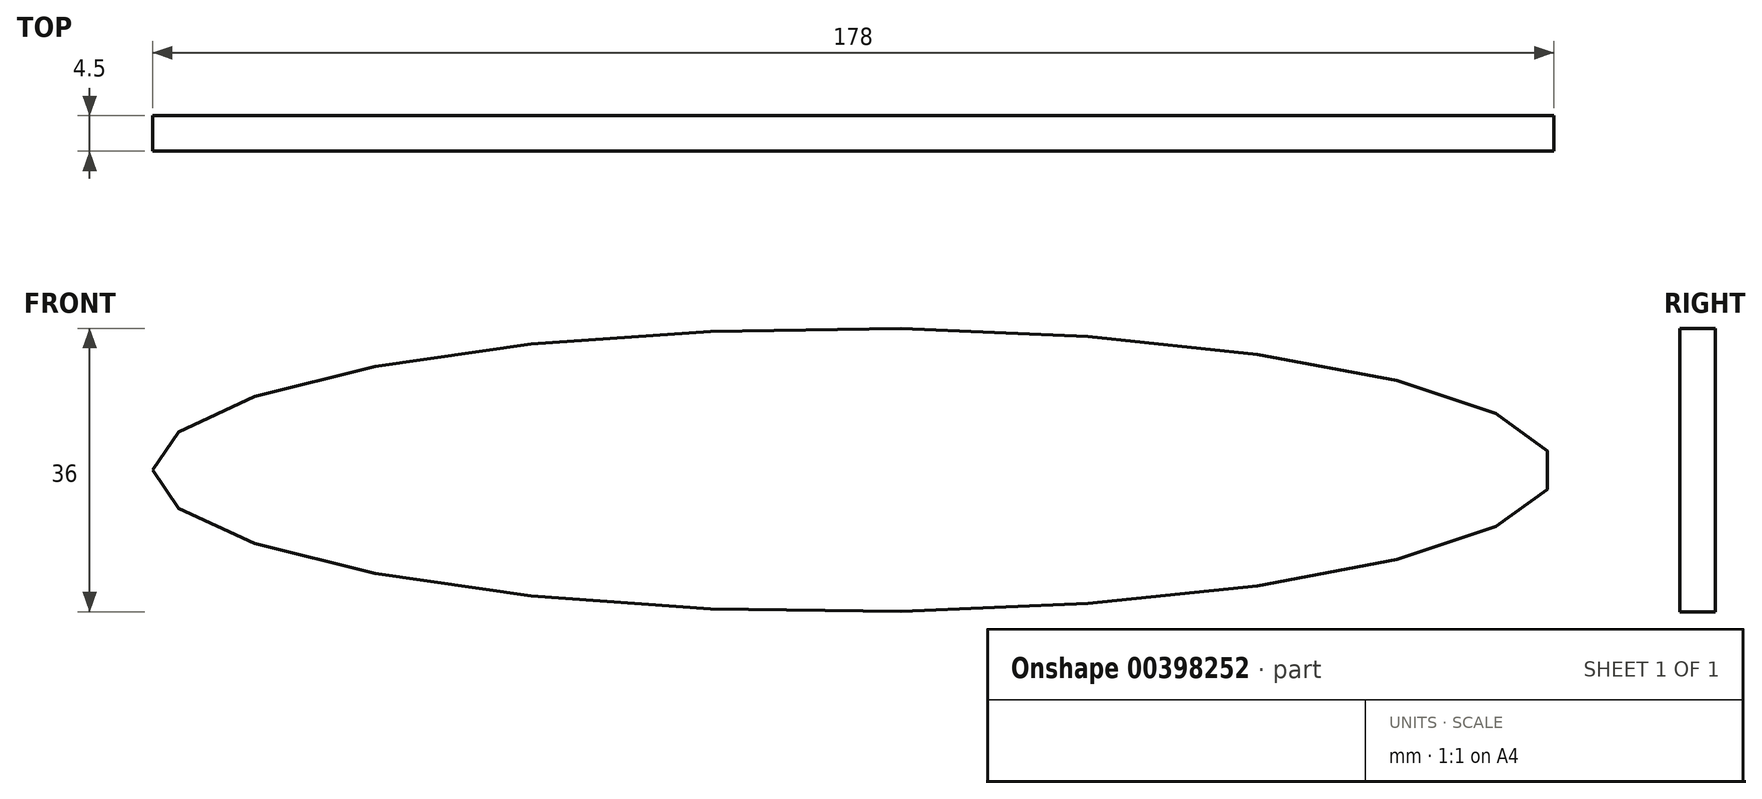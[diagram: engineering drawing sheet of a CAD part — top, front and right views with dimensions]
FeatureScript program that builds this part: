
annotation { "Feature Type Name" : "Feature", "Feature Type Description" : "" }
export const myFeature = defineFeature(function(context is Context, id is Id, definition is map)
    precondition{}
    {
        {
            var Q0;
            Q0=qCreatedBy(makeId("Front.planeOp"),FACE);
            var sketch = newSketch(context, id + "F0", { "sketchPlane" : qUnion([Q0])});
            skEllipse(sketch, "E0", {"center": v(58.81, 0) * mm, "majorRadius": 89 * mm, "minorRadius": 18 * mm, "majorAxis": v(-1, 0)});
            skSolve(sketch);
        }
        {
            var Q0;
            Q0=qSketchRegion(id+"F0",true);
            var Q1;
            Q1=makeQuery(id+"F0.imprint","IMPRINT",FACE,{"disambiguationData":[TD([[makeQuery(id+"F0.imprint","IMPRINT",EDGE,{"derivedFrom":sQuery(id+"F0.wireOp",EDGE,"E0")}),1.0]])]});
            extrude(context, id + "F1", {"entities" : qUnion([Q0, Q1]), "depth" : 1.5 * mm});
        }
        {
            var Q0;
            Q0=qCreatedBy(makeId("Front.planeOp"),FACE);
            var sketch = newSketch(context, id + "F2", { "sketchPlane" : qUnion([Q0])});
            skLineSegment(sketch, "E1", {"start": v(-9.04, 3) * mm, "end": v(11.23, 3) * mm, "construction": true});
            skLineSegment(sketch, "E2", {"start": v(-14.09, 2.99) * mm, "end": v(-14.09, 6.2) * mm});
            skLineSegment(sketch, "E3", {"start": v(-14.09, 6.2) * mm, "end": v(0, 6.2) * mm});
            skLineSegment(sketch, "E4", {"start": v(0, 6.2) * mm, "end": v(0, 10.97) * mm});
            skLineSegment(sketch, "E5", {"start": v(0, 10.97) * mm, "end": v(3.01, 10.97) * mm});
            skLineSegment(sketch, "E6", {"start": v(3.01, 10.97) * mm, "end": v(3.01, 6.2) * mm});
            skLineSegment(sketch, "E7", {"start": v(3.01, 6.2) * mm, "end": v(17.42, 6.2) * mm});
            skLineSegment(sketch, "E8", {"start": v(-14.09, 2.99) * mm, "end": v(17.42, 3) * mm});
            skLineSegment(sketch, "E9", {"start": v(17.42, 3) * mm, "end": v(17.42, 6.2) * mm});
            skLineSegment(sketch, "E10", {"start": v(0, 6.2) * mm, "end": v(0, -11.46) * mm, "construction": true});
            skLineSegment(sketch, "E11", {"start": v(9.3, -3) * mm, "end": v(17.42, -3) * mm});
            skPoint(sketch, "E11.endSnap0", {"position": v(17.42, -3.74) * mm});
            skLineSegment(sketch, "E12", {"start": v(17.42, -3) * mm, "end": v(-14.24, -3) * mm});
            skLineSegment(sketch, "E13", {"start": v(-14.24, -3) * mm, "end": v(-14.09, -6.29) * mm});
            skLineSegment(sketch, "E14", {"start": v(-14.09, -6.29) * mm, "end": v(0, -6.28) * mm});
            skLineSegment(sketch, "E15", {"start": v(0, -6.28) * mm, "end": v(0, -11.46) * mm});
            skLineSegment(sketch, "E16", {"start": v(3.02, -11.46) * mm, "end": v(3.02, -6.28) * mm});
            skLineSegment(sketch, "E17", {"start": v(3.02, -6.28) * mm, "end": v(17.42, -6.27) * mm});
            skLineSegment(sketch, "E18", {"start": v(17.42, -6.27) * mm, "end": v(17.42, -3.74) * mm});
            skLineSegment(sketch, "E19", {"start": v(3.02, -11.46) * mm, "end": v(0, -11.46) * mm});
            skLineSegment(sketch, "E20", {"start": v(17.42, -3.74) * mm, "end": v(17.42, -3) * mm});
            skSolve(sketch);
        }
        {
            var Q0;
            Q0=makeQuery(id+"F1.opExtrude","CAP_FACE",FACE,{"disambiguationData":[OSD([sQuery(id+"F0.wireOp",EDGE,"E0")])],"isStart":false});
            var Q1;
            Q1=makeQuery(id+"FVdWLll0MW8gGsK_1.opExtrude","CAP_FACE",FACE,{"disambiguationData":[OSD([sQuery(id+"F2.wireOp",EDGE,"E2"),sQuery(id+"F2.wireOp",EDGE,"E3"),sQuery(id+"F2.wireOp",EDGE,"E4"),sQuery(id+"F2.wireOp",EDGE,"E5"),sQuery(id+"F2.wireOp",EDGE,"E6"),sQuery(id+"F2.wireOp",EDGE,"E7"),sQuery(id+"F2.wireOp",EDGE,"E8"),sQuery(id+"F2.wireOp",EDGE,"E9")])],"isStart":false});
            extrude(context, id + "F3", {"entities" : qUnion([Q0, Q1]), "operationType" : NewBodyOperationType.ADD, "depth" : 3 * mm});
        }
    });
